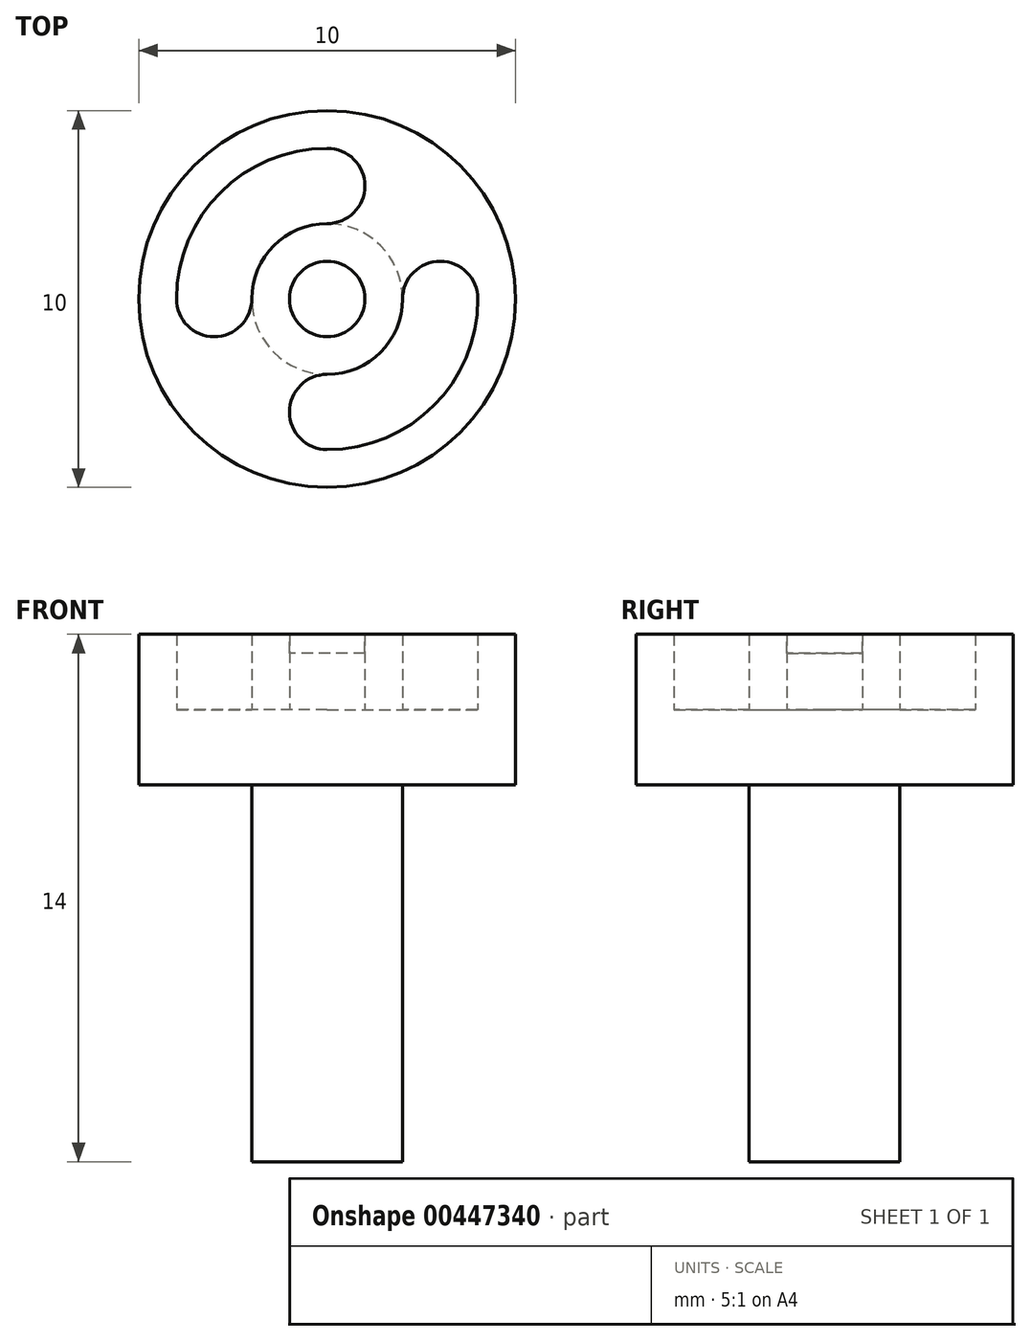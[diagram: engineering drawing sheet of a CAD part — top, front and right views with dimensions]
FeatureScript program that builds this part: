
annotation { "Feature Type Name" : "Feature", "Feature Type Description" : "" }
export const myFeature = defineFeature(function(context is Context, id is Id, definition is map)
    precondition{}
    {
        {
            var Q0;
            Q0=qCreatedBy(makeId("Top.planeOp"),FACE);
            var sketch = newSketch(context, id + "F0", { "sketchPlane" : qUnion([Q0])});
            skLineSegment(sketch, "E0", {"start": v(0.25, -12) * mm, "end": v(15.75, -12) * mm, "construction": true});
            skCircle(sketch, "E1", {"center": v(8, -12) * mm, "radius": 5 * mm});
            skArc(sketch, "E2", {"start": v(8, -16) * mm, "mid": v(10.83, -14.83) * mm, "end": v(12, -12) * mm});
            skArc(sketch, "E3", {"start": v(8, -14) * mm, "mid": v(9.41, -13.41) * mm, "end": v(10, -12) * mm});
            skCircle(sketch, "E4", {"center": v(8, -12) * mm, "radius": 1.5 * mm});
            skArc(sketch, "E5", {"start": v(7.01, -14.83) * mm, "mid": v(10.12, -14.12) * mm, "end": v(10.83, -11.01) * mm});
            skCircle(sketch, "E6", {"center": v(8, -15) * mm, "radius": 1 * mm});
            skCircle(sketch, "E7", {"center": v(5, -12) * mm, "radius": 1 * mm});
            skCircle(sketch, "E8", {"center": v(8, -9) * mm, "radius": 1 * mm});
            skCircle(sketch, "E9", {"center": v(11, -12) * mm, "radius": 1 * mm});
            skArc(sketch, "E10.trimOffspring", {"start": v(8, -10) * mm, "mid": v(6.59, -10.59) * mm, "end": v(6, -12) * mm});
            skArc(sketch, "E11.trimOffspring", {"start": v(8.99, -9.17) * mm, "mid": v(8, -9) * mm, "end": v(7.01, -9.17) * mm});
            skArc(sketch, "E12.trimOffspring", {"start": v(8, -8) * mm, "mid": v(5.17, -9.17) * mm, "end": v(4, -12) * mm});
            skArc(sketch, "E13.trimOffspring", {"start": v(5.17, -11.01) * mm, "mid": v(5, -12) * mm, "end": v(5.17, -12.99) * mm});
            skLineSegment(sketch, "E14", {"start": v(8, -12) * mm, "end": v(7.01, -9.17) * mm, "construction": true});
            skLineSegment(sketch, "E15", {"start": v(8, -12) * mm, "end": v(8.99, -9.17) * mm, "construction": true});
            skLineSegment(sketch, "E16", {"start": v(8, -12) * mm, "end": v(10.83, -11.01) * mm, "construction": true});
            skSolve(sketch);
        }
        {
            var Q0;
            Q0=makeQuery(id+"F0.imprint","IMPRINT",FACE,{"disambiguationData":[TD([[makeQuery(id+"F0.imprint","IMPRINT",EDGE,{"derivedFrom":sQuery(id+"F0.wireOp",EDGE,"E1")}),1.0]])]});
            var Q1;
            Q1=makeQuery(id+"F0.imprint","IMPRINT",FACE,{"disambiguationData":[TD([[makeQuery(id+"F0.imprint","IMPRINT",EDGE,{"derivedFrom":sQuery(id+"F0.wireOp",EDGE,"E4")}),1.0]])]});
            extrude(context, id + "F1", {"entities" : qUnion([Q0, Q1]), "depth" : 2 * mm});
        }
        {
            var Q0;
            Q0=makeQuery(id+"F0.imprint","IMPRINT",FACE,{"disambiguationData":[TD([[makeQuery(id+"F0.imprint","IMPRINT",EDGE,{"derivedFrom":sQuery(id+"F0.wireOp",EDGE,"E1")}),1.0]])]});
            var Q1;
            {var subQ0=sQuery(id+"F0.wireOp",EDGE,"E2");Q1=makeQuery(id+"F0.imprint","IMPRINT",FACE,{"disambiguationData":[TD([[makeQuery(id+"F0.imprint","IMPRINT",EDGE,{"derivedFrom":subQ0}),1.0]])]});}
            var Q2;
            {var subQ0=sQuery(id+"F0.wireOp",EDGE,"E3");Q2=makeQuery(id+"F0.imprint","IMPRINT",FACE,{"disambiguationData":[TD([[makeQuery(id+"F0.imprint","IMPRINT",EDGE,{"derivedFrom":subQ0}),-1.0]])]});}
            var Q3;
            {var subQ0=sQuery(id+"F0.wireOp",EDGE,"E9");var subQ1=sQuery(id+"F0.wireOp",EDGE,"E5");var subQ2=makeQuery(id+"F0.imprint","INTERSECT",VERTEX,{"disambiguationData":[OD(0.0)],"derivedFrom":[subQ1,subQ0]});Q3=makeQuery(id+"F0.imprint","IMPRINT",FACE,{"disambiguationData":[TD([[makeQuery(id+"F0.imprint","IMPRINT",EDGE,{"disambiguationData":[TD([[subQ2,1.0]])],"derivedFrom":subQ1}),-1.0]])]});}
            var Q4;
            {var subQ0=sQuery(id+"F0.wireOp",EDGE,"E9");var subQ1=sQuery(id+"F0.wireOp",EDGE,"E5");var subQ2=makeQuery(id+"F0.imprint","INTERSECT",VERTEX,{"disambiguationData":[OD(0.0)],"derivedFrom":[subQ1,subQ0]});Q4=makeQuery(id+"F0.imprint","IMPRINT",FACE,{"disambiguationData":[TD([[makeQuery(id+"F0.imprint","IMPRINT",EDGE,{"disambiguationData":[TD([[subQ2,1.0]])],"derivedFrom":subQ1}),1.0]])]});}
            var Q5;
            {var subQ0=sQuery(id+"F0.wireOp",EDGE,"E6");var subQ1=sQuery(id+"F0.wireOp",EDGE,"E5");var subQ2=makeQuery(id+"F0.imprint","INTERSECT",VERTEX,{"disambiguationData":[OD(0.0)],"derivedFrom":[subQ1,subQ0]});Q5=makeQuery(id+"F0.imprint","IMPRINT",FACE,{"disambiguationData":[TD([[makeQuery(id+"F0.imprint","IMPRINT",EDGE,{"disambiguationData":[TD([[subQ2,-1.0]])],"derivedFrom":subQ1}),1.0]])]});}
            var Q6;
            {var subQ0=sQuery(id+"F0.wireOp",EDGE,"E6");var subQ1=sQuery(id+"F0.wireOp",EDGE,"E5");var subQ2=makeQuery(id+"F0.imprint","INTERSECT",VERTEX,{"disambiguationData":[OD(0.0)],"derivedFrom":[subQ1,subQ0]});Q6=makeQuery(id+"F0.imprint","IMPRINT",FACE,{"disambiguationData":[TD([[makeQuery(id+"F0.imprint","IMPRINT",EDGE,{"disambiguationData":[TD([[subQ2,-1.0]])],"derivedFrom":subQ1}),-1.0]])]});}
            var Q7;
            {var subQ2=sQuery(id+"F0.wireOp",EDGE,"E11.trimOffspring");Q7=makeQuery(id+"F0.imprint","IMPRINT",FACE,{"disambiguationData":[TD([[makeQuery(id+"F0.imprint","IMPRINT",EDGE,{"derivedFrom":subQ2}),1.0]])]});}
            var Q8;
            {var subQ0=sQuery(id+"F0.wireOp",EDGE,"E11.trimOffspring");Q8=makeQuery(id+"F0.imprint","IMPRINT",FACE,{"disambiguationData":[TD([[makeQuery(id+"F0.imprint","IMPRINT",EDGE,{"derivedFrom":subQ0}),-1.0]])]});}
            var Q9;
            {var subQ5=sQuery(id+"F0.wireOp",EDGE,"E10.trimOffspring");Q9=makeQuery(id+"F0.imprint","IMPRINT",FACE,{"disambiguationData":[TD([[makeQuery(id+"F0.imprint","IMPRINT",EDGE,{"derivedFrom":subQ5}),-1.0]])]});}
            var Q10;
            {var subQ2=sQuery(id+"F0.wireOp",EDGE,"E13.trimOffspring");Q10=makeQuery(id+"F0.imprint","IMPRINT",FACE,{"disambiguationData":[TD([[makeQuery(id+"F0.imprint","IMPRINT",EDGE,{"derivedFrom":subQ2}),1.0]])]});}
            var Q11;
            {var subQ2=sQuery(id+"F0.wireOp",EDGE,"E13.trimOffspring");Q11=makeQuery(id+"F0.imprint","IMPRINT",FACE,{"disambiguationData":[TD([[makeQuery(id+"F0.imprint","IMPRINT",EDGE,{"derivedFrom":subQ2}),-1.0]])]});}
            extrude(context, id + "F2", {"entities" : qUnion([Q0, Q1, Q2, Q3, Q4, Q5, Q6, Q7, Q8, Q9, Q10, Q11]), "operationType" : NewBodyOperationType.ADD, "oppositeDirection" : true, "depth" : 2 * mm});
        }
        {
            var Q0;
            Q0=makeQuery(id+"F0.imprint","IMPRINT",FACE,{"disambiguationData":[TD([[makeQuery(id+"F0.imprint","IMPRINT",EDGE,{"derivedFrom":sQuery(id+"F0.wireOp",EDGE,"E4")}),1.0]])]});
            extrude(context, id + "F3", {"entities" : qUnion([Q0]), "operationType" : NewBodyOperationType.ADD, "oppositeDirection" : true, "depth" : 2 * mm});
        }
        {
            var Q0;
            {var subQ0=sQuery(id+"F0.wireOp",EDGE,"E4");Q0=makeQuery(id+"F3.boolean.opBoolean","MERGE",FACE,{"derivedFrom":[makeQuery(id+"F2.opExtrude","CAP_FACE",FACE,{"disambiguationData":[OSD([sQuery(id+"F0.wireOp",EDGE,"E1"),subQ0])],"isStart":false}),makeQuery(id+"F3.opExtrude","CAP_FACE",FACE,{"disambiguationData":[OSD([subQ0])],"isStart":false})]});}
            var sketch = newSketch(context, id + "F4", { "sketchPlane" : qUnion([Q0])});
            skCircle(sketch, "E17", {"center": v(8, 12) * mm, "radius": 2 * mm});
            skSolve(sketch);
        }
        {
            var Q0;
            Q0=makeQuery(id+"F4.imprint","IMPRINT",FACE,{"disambiguationData":[TD([[makeQuery(id+"F4.imprint","IMPRINT",EDGE,{"derivedFrom":sQuery(id+"F4.wireOp",EDGE,"E17")}),1.0]])]});
            extrude(context, id + "F5", {"entities" : qUnion([Q0]), "operationType" : NewBodyOperationType.ADD, "depth" : 10 * mm});
        }
        {
            var Q0;
            Q0=makeQuery(id+"F1.opExtrude","CAP_FACE",FACE,{"disambiguationData":[OSD([sQuery(id+"F0.wireOp",EDGE,"E1"),sQuery(id+"F0.wireOp",EDGE,"E2"),sQuery(id+"F0.wireOp",EDGE,"E3"),sQuery(id+"F0.wireOp",EDGE,"E6"),sQuery(id+"F0.wireOp",EDGE,"E7"),sQuery(id+"F0.wireOp",EDGE,"E8"),sQuery(id+"F0.wireOp",EDGE,"E9"),sQuery(id+"F0.wireOp",EDGE,"E10.trimOffspring"),sQuery(id+"F0.wireOp",EDGE,"E12.trimOffspring")])],"isStart":false});
            var sketch = newSketch(context, id + "F6", { "sketchPlane" : qUnion([Q0])});
            skCircle(sketch, "E18", {"center": v(8, -12) * mm, "radius": 1 * mm});
            skSolve(sketch);
        }
        {
            var Q0;
            Q0=makeQuery(id+"F6.imprint","IMPRINT",FACE,{"disambiguationData":[TD([[makeQuery(id+"F6.imprint","IMPRINT",EDGE,{"derivedFrom":sQuery(id+"F6.wireOp",EDGE,"E18")}),1.0]])]});
            extrude(context, id + "F7", {"entities" : qUnion([Q0]), "operationType" : NewBodyOperationType.REMOVE, "oppositeDirection" : true, "depth" : .5 * mm});
        }
    });
